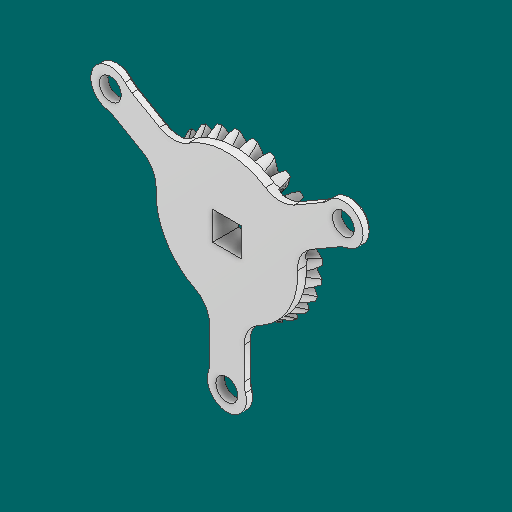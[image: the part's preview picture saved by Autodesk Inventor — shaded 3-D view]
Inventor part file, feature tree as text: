
AUTODESK INVENTOR PART (.ipt)
format: ipt  version: 2023.1 (Build 271208000, 208)  size: 766,464 bytes
history: native  units: in
note: dims shown in document units (in); Inventor stores cm internally (conversion verified against a paired STEP export)
features: other x30, sketch x3
ambient origin geometry x8: Origin, YZ Plane, XZ Plane, XY Plane, X Axis, Y Axis, Z Axis, Center Point
bodies: Solid1 (feature_tree)
feature tree (33):
  other  "Bevel Gear2"
  other  "Solid1::Bevel Gear2"
  other  "TaggingFeature1"
  other  "Teeth Body Sketch"
  other  "Start Sketch"
  other  "End Sketch"
  other  "End Sketch Right"
  other  "End Sketch Left"
  other  "Body Sketch"
  sketch  "Sketch6"  dims[d0=0.3937in]
  sketch  "Sketch8"  dims[d48=0.0in]
  sketch  "Sketch9"  dims[d49=0.0in d50=90.0deg d52=0.0in d53=0.0in d54=0.0in]
  other  "3D Sketch Right"
  other  "3D Sketch Left"
  other  "Mesh Plane"
  other  "Top Plane"
  other  "Mesh Plane2"
  other  "Tooth Plane"
  other  "End Plane"
  other  "End Plane Right"
  other  "End Plane Left"
  other  "Z Axis_1"
  other  "Top Point"
  other  "Start Point"
  other  "End Point"
  other  "Srf1"
  other  "Srf1::Derived"
  other  "Start plane iMate"
  other  "Mesh iMate2"
  other  "Axis Angle iMate"
  other  "Axis iMate"
  other  "Mesh iMate"
  other  "Intersection iMate"
